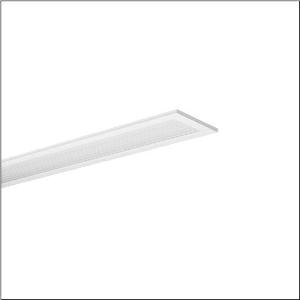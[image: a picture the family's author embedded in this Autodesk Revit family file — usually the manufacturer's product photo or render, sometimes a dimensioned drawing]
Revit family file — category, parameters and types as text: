
# Revit family: apollon_r__21_linear_51mq16wm2414_a263
name_source: partatom
category: Lighting Fixtures
units: mm (PartAtom-declared; Revit-internal decimal feet)

## family parameters
Cut with Voids When Loaded = No
Host = Face
Light Source = No
Part Type = Normal
Room Calculation Point = No
Round Connector Dimension = Use Diameter
Shared = No

## types (1)
- --- (1 x LED, 4380 lm, 29.4 W, 4000K)
    Apparent Load = 29 VA
    CIE Flux Codes = 64 88 97 100 100
    Color Rendering = 80
    Color Temperature = 4000K
    Default Elevation = 1800 mm
    Description = Apollon® 21 linear, office luminaire, primary optical cover: micro prismatic cover, of PMMA, CAT 2 (L<= 3000cd/m²), light emission: direct distribution, primary light characteristic: symmetric, installation type: lay-in mounting, LED, rated luminous flux: 3.520lm, luminous efficacy: 151lm/W, light colour: 840, colour temperature: 4000K, with terminal, 3-pole, mains connection: 220..240V, AC/DC, 0/50..60Hz, rated input power: 23.4W, housing, of aluminium, coated, traffic white (RAL 9016), length: 1.545mm, width: 179mm, height: 30mm, housing upper side, of sheet steel, galvanised, protection rating (complete): IP20, protection rating (lamp compartment, on room side): IP50, insulation class (complete): insulation class II (safety insulation), certification: CE, ENEC, impact resistance: IK03, permissible operating ambient temperature: -20..+45°C, permissible storage temperature: -40..+80°C, packaging unit: 1 piece
    Height = 0 mm  [stored 0 ft]
    Lamp = 1 x LED
    Lamp Light Flux = 4380 lm
    Lamp Power = 29.4 W
    Lamp count = 1
    Length = 1545 mm
    Luminous efficacy = 149 lm/W
    Manufacturer = Siteco
    ModVariant = No
    Model = 51MQ16WM2414
    Mounting Place = Ceiling
    Mounting Type = Recessed
    Number of Poles = 1
    OnlyDefault = Yes
    Power Factor = 1
    Product Name = Apollon® 21 linear
    Product group = office luminaire | ceiling recessed
    ProductGroupID = 401
    Protection Class = Protection class II
    Protection Degree = IP 20
    RLX_Detail_Level = 1
    RLX_Emergency_Light_Flux = 0 lm
    RLX_Emergency_Type = 0
    RLX_Emergency_Type_DB = No
    RlxData = <blob elided: 13873 chars, md5=26f39a19>
    Socket = socket
    Standby Power = 0 W
    System Light Flux = 4380 lm
    System Power = 29 W
    Type Comments = factory setting: luminous flux: 100 % | (ON | ON | ON) | 700 mA
    Type Image = l_1291018.jpg
    URL = http://relux.com
    VarID = @adj_023333
    Voltage = 0 V
    Weight = 0.00 kg
    Width = 179 mm

note: [stored X ft] marks values corroborated as IEEE doubles in the binary element streams (Revit-internal decimal feet)

## geometry (parser evidence)
native form markers: Sweep x10
no freeform markers — native parametric forms only
